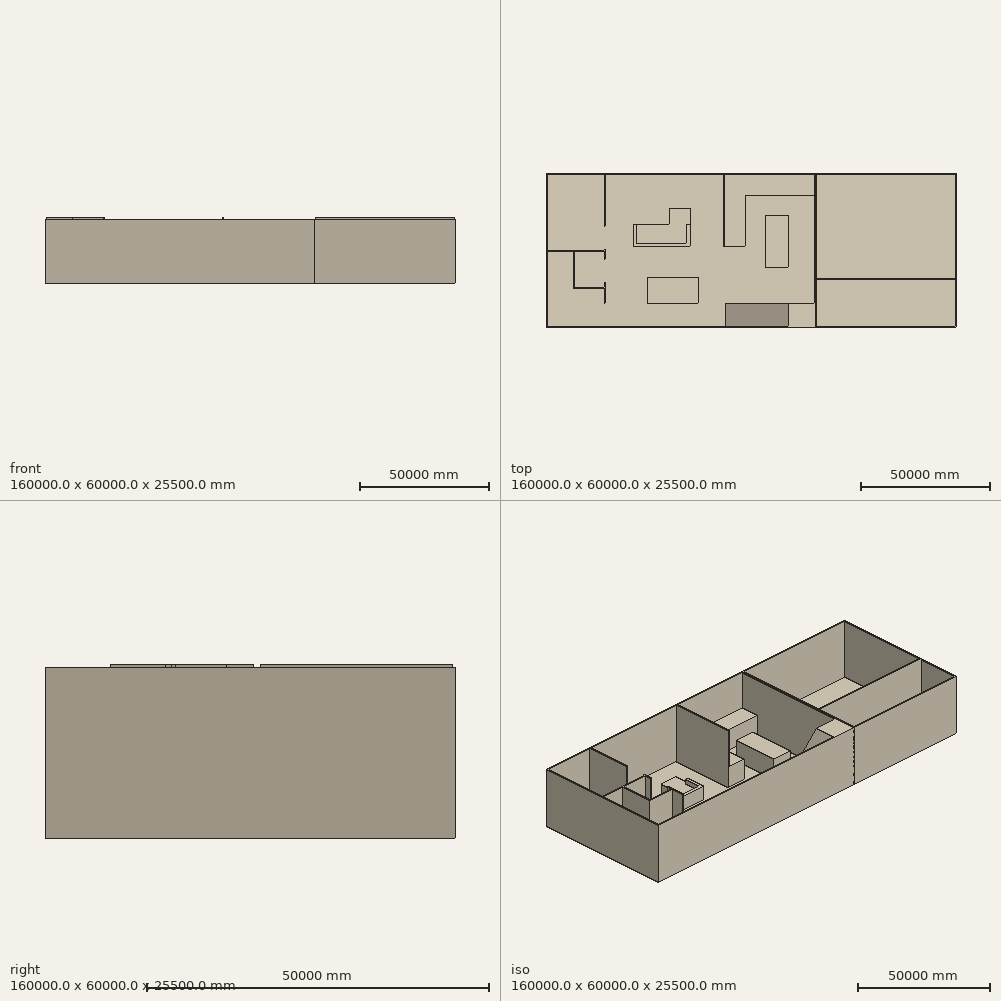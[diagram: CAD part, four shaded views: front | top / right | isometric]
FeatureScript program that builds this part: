
annotation { "Feature Type Name" : "Feature", "Feature Type Description" : "" }
export const myFeature = defineFeature(function(context is Context, id is Id, definition is map)
    precondition{}
    {
        {
            var Q0;
            Q0=qCreatedBy(makeId("Top.planeOp"),FACE);
            var sketch = newSketch(context, id + "F0", { "sketchPlane" : qUnion([Q0])});
            skLineSegment(sketch, "E0.bottom", {"start": v(52500, 30000) * mm, "end": v(-52500, 30000) * mm});
            skLineSegment(sketch, "E0.top", {"start": v(52500, -30000) * mm, "end": v(-52500, -30000) * mm});
            skLineSegment(sketch, "E0.left", {"start": v(52500, 30000) * mm, "end": v(52500, -30000) * mm});
            skLineSegment(sketch, "E0.right", {"start": v(-52500, 30000) * mm, "end": v(-52500, -30000) * mm});
            skPoint(sketch, "E0.middle", {"position": v(0, 0) * mm});
            skSolve(sketch);
        }
        {
            var Q0;
            Q0 = qSketchRegion(id + "F0", true);
            extrude(context, id + "F1", {"entities" : qUnion([Q0]), "depth" : 25000 * mm, "offsetDistance" : 25 * mm});
        }
        {
            var Q0;
            Q0=makeQuery(id+"F1.opExtrude","CAP_FACE",FACE,{"disambiguationData":[OSD([sQuery(id+"F0.wireOp",EDGE,"E0.bottom"),sQuery(id+"F0.wireOp",EDGE,"E0.top"),sQuery(id+"F0.wireOp",EDGE,"E0.left"),sQuery(id+"F0.wireOp",EDGE,"E0.right")])],"isStart":false});
            shell(context, id + "F2", {"entities" : qUnion([Q0]), "thickness" : 500 * mm});
        }
        {
            var Q0;
            Q0=makeQuery(id+"F2.opShell","OFFSET_FACE",FACE,{"disambiguationData":[OSD([sQuery(id+"F0.wireOp",EDGE,"E0.bottom"),sQuery(id+"F0.wireOp",EDGE,"E0.top"),sQuery(id+"F0.wireOp",EDGE,"E0.left"),sQuery(id+"F0.wireOp",EDGE,"E0.right")])]});
            var sketch = newSketch(context, id + "F3", { "sketchPlane" : qUnion([Q0])});
            skLineSegment(sketch, "E1", {"start": v(-29500, 29500) * mm, "end": v(-29500, 9500) * mm});
            skLineSegment(sketch, "E2", {"start": v(-29500, 9500) * mm, "end": v(-30000, 9500) * mm});
            skLineSegment(sketch, "E3", {"start": v(-30000, 9500) * mm, "end": v(-30000, 29500) * mm});
            skLineSegment(sketch, "E4", {"start": v(-30000, 29500) * mm, "end": v(-29500, 29500) * mm});
            skLineSegment(sketch, "E5.bottom", {"start": v(-29500, 500) * mm, "end": v(-30000, 500) * mm});
            skLineSegment(sketch, "E5.top", {"start": v(-29500, -3500) * mm, "end": v(-30000, -3500) * mm});
            skLineSegment(sketch, "E5.left", {"start": v(-29500, 500) * mm, "end": v(-29500, -3500) * mm});
            skLineSegment(sketch, "E6.bottom", {"start": v(-30000, -12500) * mm, "end": v(-29500, -12500) * mm});
            skLineSegment(sketch, "E6.top", {"start": v(-30000, -20500) * mm, "end": v(-29500, -20500) * mm});
            skLineSegment(sketch, "E6.right", {"start": v(-29500, -20500) * mm, "end": v(-29500, -12500) * mm});
            skLineSegment(sketch, "E7", {"start": v(-30000, -12500) * mm, "end": v(-30000, -14500) * mm});
            skLineSegment(sketch, "E8", {"start": v(-30000, -14500) * mm, "end": v(-41500, -14500) * mm});
            skLineSegment(sketch, "E9", {"start": v(-41500, -14500) * mm, "end": v(-41500, -500) * mm});
            skLineSegment(sketch, "E10", {"start": v(-41500, -500) * mm, "end": v(-30000, -500) * mm});
            skLineSegment(sketch, "E11", {"start": v(-30000, -3500) * mm, "end": v(-30000, -500) * mm});
            skLineSegment(sketch, "E12", {"start": v(-30000, 500) * mm, "end": v(-30000, 0) * mm});
            skLineSegment(sketch, "E13", {"start": v(-30000, 0) * mm, "end": v(-52000, 0) * mm});
            skLineSegment(sketch, "E14", {"start": v(-42000, -15000) * mm, "end": v(-30000, -15000) * mm});
            skLineSegment(sketch, "E15", {"start": v(-30000, -15000) * mm, "end": v(-30000, -20500) * mm});
            skLineSegment(sketch, "E16", {"start": v(-42000, -15000) * mm, "end": v(-42000, -500) * mm});
            skLineSegment(sketch, "E17", {"start": v(-42000, -500) * mm, "end": v(-52000, -500) * mm});
            skLineSegment(sketch, "E18", {"start": v(-52000, -500) * mm, "end": v(-52000, 0) * mm});
            skLineSegment(sketch, "E19.bottom", {"start": v(17000, 29500) * mm, "end": v(16500, 29500) * mm});
            skLineSegment(sketch, "E19.top", {"start": v(17000, 1500) * mm, "end": v(16500, 1500) * mm});
            skLineSegment(sketch, "E19.left", {"start": v(17000, 29500) * mm, "end": v(17000, 1500) * mm});
            skLineSegment(sketch, "E19.right", {"start": v(16500, 29500) * mm, "end": v(16500, 1500) * mm});
            skSolve(sketch);
        }
        {
            var Q0;
            Q0 = qSketchRegion(id + "F3", true);
            extrude(context, id + "F4", {"entities" : qUnion([Q0]), "operationType" : NewBodyOperationType.ADD, "depth" : 25000 * mm, "offsetDistance" : 25 * mm});
        }
        {
            var Q0;
            Q0=makeQuery(id+"F2.opShell","OFFSET_FACE",FACE,{"disambiguationData":[OSD([sQuery(id+"F0.wireOp",EDGE,"E0.bottom"),sQuery(id+"F0.wireOp",EDGE,"E0.top"),sQuery(id+"F0.wireOp",EDGE,"E0.left"),sQuery(id+"F0.wireOp",EDGE,"E0.right")])]});
            var sketch = newSketch(context, id + "F5", { "sketchPlane" : qUnion([Q0])});
            skLineSegment(sketch, "E20", {"start": v(17000, 1500) * mm, "end": v(25000, 1500) * mm});
            skLineSegment(sketch, "E21", {"start": v(25000, 1500) * mm, "end": v(25000, 21500) * mm});
            skLineSegment(sketch, "E22", {"start": v(25000, 21500) * mm, "end": v(52000, 21500) * mm});
            skLineSegment(sketch, "E23", {"start": v(52000, 21500) * mm, "end": v(52000, 29500) * mm});
            skLineSegment(sketch, "E24", {"start": v(52000, 29500) * mm, "end": v(17000, 29500) * mm});
            skLineSegment(sketch, "E25", {"start": v(17000, 29500) * mm, "end": v(17000, 1500) * mm});
            skLineSegment(sketch, "E26.bottom", {"start": v(33000, -6500) * mm, "end": v(42000, -6500) * mm});
            skLineSegment(sketch, "E26.top", {"start": v(33000, 13500) * mm, "end": v(42000, 13500) * mm});
            skLineSegment(sketch, "E26.left", {"start": v(33000, -6500) * mm, "end": v(33000, 13500) * mm});
            skLineSegment(sketch, "E26.right", {"start": v(42000, -6500) * mm, "end": v(42000, 13500) * mm});
            skSolve(sketch);
        }
        {
            var Q0;
            Q0 = qSketchRegion(id + "F5", true);
            extrude(context, id + "F6", {"entities" : qUnion([Q0]), "operationType" : NewBodyOperationType.ADD, "depth" : 9000 * mm, "offsetDistance" : 25 * mm});
        }
        {
            var Q0;
            Q0=makeQuery(id+"F2.opShell","OFFSET_FACE",FACE,{"disambiguationData":[OSD([sQuery(id+"F0.wireOp",EDGE,"E0.bottom"),sQuery(id+"F0.wireOp",EDGE,"E0.top"),sQuery(id+"F0.wireOp",EDGE,"E0.left"),sQuery(id+"F0.wireOp",EDGE,"E0.right")])]});
            var sketch = newSketch(context, id + "F7", { "sketchPlane" : qUnion([Q0])});
            skLineSegment(sketch, "E27.bottom", {"start": v(-13000, -20500) * mm, "end": v(-11000, -20500) * mm});
            skLineSegment(sketch, "E27.top", {"start": v(-13000, -18500) * mm, "end": v(-11000, -18500) * mm});
            skLineSegment(sketch, "E27.left", {"start": v(-13000, -20500) * mm, "end": v(-13000, -18500) * mm});
            skLineSegment(sketch, "E27.right", {"start": v(-11000, -20500) * mm, "end": v(-11000, -18500) * mm});
            skLineSegment(sketch, "E28.bottom", {"start": v(-13000, -10500) * mm, "end": v(-11000, -10500) * mm});
            skLineSegment(sketch, "E28.top", {"start": v(-13000, -12500) * mm, "end": v(-11000, -12500) * mm});
            skLineSegment(sketch, "E28.left", {"start": v(-13000, -10500) * mm, "end": v(-13000, -12500) * mm});
            skLineSegment(sketch, "E28.right", {"start": v(-11000, -10500) * mm, "end": v(-11000, -12500) * mm});
            skLineSegment(sketch, "E29.bottom", {"start": v(5000, -10500) * mm, "end": v(7000, -10500) * mm});
            skLineSegment(sketch, "E29.top", {"start": v(5000, -12500) * mm, "end": v(7000, -12500) * mm});
            skLineSegment(sketch, "E29.left", {"start": v(5000, -10500) * mm, "end": v(5000, -12500) * mm});
            skLineSegment(sketch, "E29.right", {"start": v(7000, -10500) * mm, "end": v(7000, -12500) * mm});
            skLineSegment(sketch, "E30.bottom", {"start": v(5000, -18500) * mm, "end": v(7000, -18500) * mm});
            skLineSegment(sketch, "E30.top", {"start": v(5000, -20500) * mm, "end": v(7000, -20500) * mm});
            skLineSegment(sketch, "E30.left", {"start": v(5000, -18500) * mm, "end": v(5000, -20500) * mm});
            skLineSegment(sketch, "E30.right", {"start": v(7000, -18500) * mm, "end": v(7000, -20500) * mm});
            skSolve(sketch);
        }
        {
            var Q0;
            Q0 = qSketchRegion(id + "F7", true);
            extrude(context, id + "F8", {"entities" : qUnion([Q0]), "operationType" : NewBodyOperationType.ADD, "depth" : 7000 * mm, "offsetDistance" : 25 * mm});
        }
        {
            var Q0;
            Q0=makeQuery(id+"F8.opExtrude","CAP_FACE",FACE,{"disambiguationData":[OSD([sQuery(id+"F7.wireOp",EDGE,"E28.bottom"),sQuery(id+"F7.wireOp",EDGE,"E28.top"),sQuery(id+"F7.wireOp",EDGE,"E28.left"),sQuery(id+"F7.wireOp",EDGE,"E28.right")])],"isStart":false});
            var sketch = newSketch(context, id + "F9", { "sketchPlane" : qUnion([Q0])});
            skLineSegment(sketch, "E31.bottom", {"start": v(-13000, -10500) * mm, "end": v(7000, -10500) * mm});
            skLineSegment(sketch, "E31.top", {"start": v(-13000, -20500) * mm, "end": v(7000, -20500) * mm});
            skLineSegment(sketch, "E31.left", {"start": v(-13000, -10500) * mm, "end": v(-13000, -20500) * mm});
            skLineSegment(sketch, "E31.right", {"start": v(7000, -10500) * mm, "end": v(7000, -20500) * mm});
            skSolve(sketch);
        }
        {
            var Q0;
            Q0 = qSketchRegion(id + "F9", true);
            extrude(context, id + "F10", {"entities" : qUnion([Q0]), "operationType" : NewBodyOperationType.ADD, "depth" : 1000 * mm, "offsetDistance" : 25 * mm});
        }
        {
            var Q0;
            Q0=makeQuery(id+"F2.opShell","OFFSET_FACE",FACE,{"disambiguationData":[OSD([sQuery(id+"F0.wireOp",EDGE,"E0.bottom"),sQuery(id+"F0.wireOp",EDGE,"E0.top"),sQuery(id+"F0.wireOp",EDGE,"E0.left"),sQuery(id+"F0.wireOp",EDGE,"E0.right")])]});
            var sketch = newSketch(context, id + "F11", { "sketchPlane" : qUnion([Q0])});
            skLineSegment(sketch, "E32", {"start": v(-18500, 10000) * mm, "end": v(-4500, 10000) * mm});
            skLineSegment(sketch, "E33", {"start": v(-4500, 10000) * mm, "end": v(-4500, 16500) * mm});
            skLineSegment(sketch, "E34", {"start": v(-4500, 16500) * mm, "end": v(3500, 16500) * mm});
            skLineSegment(sketch, "E35", {"start": v(3500, 16500) * mm, "end": v(3500, 1500) * mm});
            skLineSegment(sketch, "E36", {"start": v(3500, 1500) * mm, "end": v(-18500, 1500) * mm});
            skLineSegment(sketch, "E37", {"start": v(-18500, 1500) * mm, "end": v(-18500, 10000) * mm});
            skSolve(sketch);
        }
        {
            var Q0;
            Q0 = qSketchRegion(id + "F11", true);
            extrude(context, id + "F12", {"entities" : qUnion([Q0]), "operationType" : NewBodyOperationType.ADD, "depth" : 4000 * mm, "offsetDistance" : 25 * mm});
        }
        {
            var Q0;
            Q0=makeQuery(id+"F12.opExtrude","CAP_FACE",FACE,{"disambiguationData":[OSD([sQuery(id+"F11.wireOp",EDGE,"E32"),sQuery(id+"F11.wireOp",EDGE,"E33"),sQuery(id+"F11.wireOp",EDGE,"E34"),sQuery(id+"F11.wireOp",EDGE,"E35"),sQuery(id+"F11.wireOp",EDGE,"E36"),sQuery(id+"F11.wireOp",EDGE,"E37")])],"isStart":false});
            var sketch = newSketch(context, id + "F13", { "sketchPlane" : qUnion([Q0])});
            skLineSegment(sketch, "E38", {"start": v(-18500, 10000) * mm, "end": v(-18500, 1500) * mm});
            skLineSegment(sketch, "E39", {"start": v(-18500, 1500) * mm, "end": v(3500, 1500) * mm});
            skLineSegment(sketch, "E40", {"start": v(3500, 1500) * mm, "end": v(3500, 10000) * mm});
            skPoint(sketch, "E40.endSnap0", {"position": v(3500, 9000) * mm});
            skLineSegment(sketch, "E41", {"start": v(3500, 10000) * mm, "end": v(2200, 10000) * mm});
            skLineSegment(sketch, "E42", {"start": v(2200, 10000) * mm, "end": v(2200, 2881.03) * mm});
            skLineSegment(sketch, "E43", {"start": v(2200, 2881.03) * mm, "end": v(-17200, 2881.03) * mm});
            skLineSegment(sketch, "E44", {"start": v(-17200, 2881.03) * mm, "end": v(-17200, 10000) * mm});
            skLineSegment(sketch, "E45", {"start": v(-17200, 10000) * mm, "end": v(-18500, 10000) * mm});
            skSolve(sketch);
        }
        {
            var Q0;
            Q0 = qSketchRegion(id + "F13", true);
            extrude(context, id + "F14", {"entities" : qUnion([Q0]), "operationType" : NewBodyOperationType.ADD, "depth" : 2000 * mm, "offsetDistance" : 25 * mm});
        }
        {
            var Q0;
            Q0=makeQuery(id+"F2.opShell","OFFSET_FACE",FACE,{"disambiguationData":[OSD([sQuery(id+"F0.wireOp",EDGE,"E0.bottom"),sQuery(id+"F0.wireOp",EDGE,"E0.top"),sQuery(id+"F0.wireOp",EDGE,"E0.left"),sQuery(id+"F0.wireOp",EDGE,"E0.right")])]});
            var sketch = newSketch(context, id + "F15", { "sketchPlane" : qUnion([Q0])});
            skLineSegment(sketch, "E46.bottom", {"start": v(52000, -29500) * mm, "end": v(17000, -29500) * mm});
            skLineSegment(sketch, "E46.top", {"start": v(52000, -20500) * mm, "end": v(17000, -20500) * mm});
            skLineSegment(sketch, "E46.left", {"start": v(52000, -29500) * mm, "end": v(52000, -20500) * mm});
            skLineSegment(sketch, "E46.right", {"start": v(17000, -29500) * mm, "end": v(17000, -20500) * mm});
            skSolve(sketch);
        }
        {
            var Q0;
            Q0 = qSketchRegion(id + "F15", true);
            extrude(context, id + "F16", {"entities" : qUnion([Q0]), "operationType" : NewBodyOperationType.ADD, "depth" : 24500 * mm, "offsetDistance" : 25 * mm});
        }
        {
            var Q0;
            Q0=makeQuery(id+"F16.opExtrude","CAP_EDGE",EDGE,{"disambiguationData":[OSD([sQuery(id+"F15.wireOp",EDGE,"E46.right")])],"isStart":false});
            chamfer(context, id + "F17", {"entities" : qUnion([Q0]), "width" : 25000 * mm, "tangentPropagation" : true});
        }
        {
            var Q0;
            Q0=qCreatedBy(makeId("Top.planeOp"),FACE);
            var sketch = newSketch(context, id + "F18", { "sketchPlane" : qUnion([Q0])});
            skLineSegment(sketch, "E47.bottom", {"start": v(52500, -30000) * mm, "end": v(107500, -30000) * mm});
            skLineSegment(sketch, "E47.top", {"start": v(52500, 30000) * mm, "end": v(107500, 30000) * mm});
            skLineSegment(sketch, "E47.left", {"start": v(52500, -30000) * mm, "end": v(52500, 30000) * mm});
            skLineSegment(sketch, "E47.right", {"start": v(107500, -30000) * mm, "end": v(107500, 30000) * mm});
            skSolve(sketch);
        }
        {
            var Q0;
            Q0 = qSketchRegion(id + "F18", true);
            extrude(context, id + "F19", {"entities" : qUnion([Q0]), "depth" : 25000 * mm, "offsetDistance" : 25 * mm});
        }
        {
            var Q0;
            Q0=makeQuery(id+"F19.opExtrude","CAP_FACE",FACE,{"disambiguationData":[OSD([sQuery(id+"F18.wireOp",EDGE,"E47.bottom"),sQuery(id+"F18.wireOp",EDGE,"E47.top"),sQuery(id+"F18.wireOp",EDGE,"E47.left"),sQuery(id+"F18.wireOp",EDGE,"E47.right")])],"isStart":false});
            shell(context, id + "F20", {"entities" : qUnion([Q0]), "thickness" : 500 * mm});
        }
        {
            var Q0;
            Q0=makeQuery(id+"F20.opShell","OFFSET_FACE",FACE,{"disambiguationData":[OSD([sQuery(id+"F18.wireOp",EDGE,"E47.bottom"),sQuery(id+"F18.wireOp",EDGE,"E47.top"),sQuery(id+"F18.wireOp",EDGE,"E47.left"),sQuery(id+"F18.wireOp",EDGE,"E47.right")])]});
            var sketch = newSketch(context, id + "F21", { "sketchPlane" : qUnion([Q0])});
            skLineSegment(sketch, "E48.bottom", {"start": v(53000, -11000) * mm, "end": v(107000, -11000) * mm});
            skLineSegment(sketch, "E48.top", {"start": v(53000, -11500) * mm, "end": v(107000, -11500) * mm});
            skLineSegment(sketch, "E48.left", {"start": v(53000, -11000) * mm, "end": v(53000, -11500) * mm});
            skLineSegment(sketch, "E48.right", {"start": v(107000, -11000) * mm, "end": v(107000, -11500) * mm});
            skSolve(sketch);
        }
        {
            var Q0;
            Q0 = qSketchRegion(id + "F21", true);
            extrude(context, id + "F22", {"entities" : qUnion([Q0]), "operationType" : NewBodyOperationType.ADD, "depth" : 25000 * mm, "offsetDistance" : 25 * mm});
        }
    });
